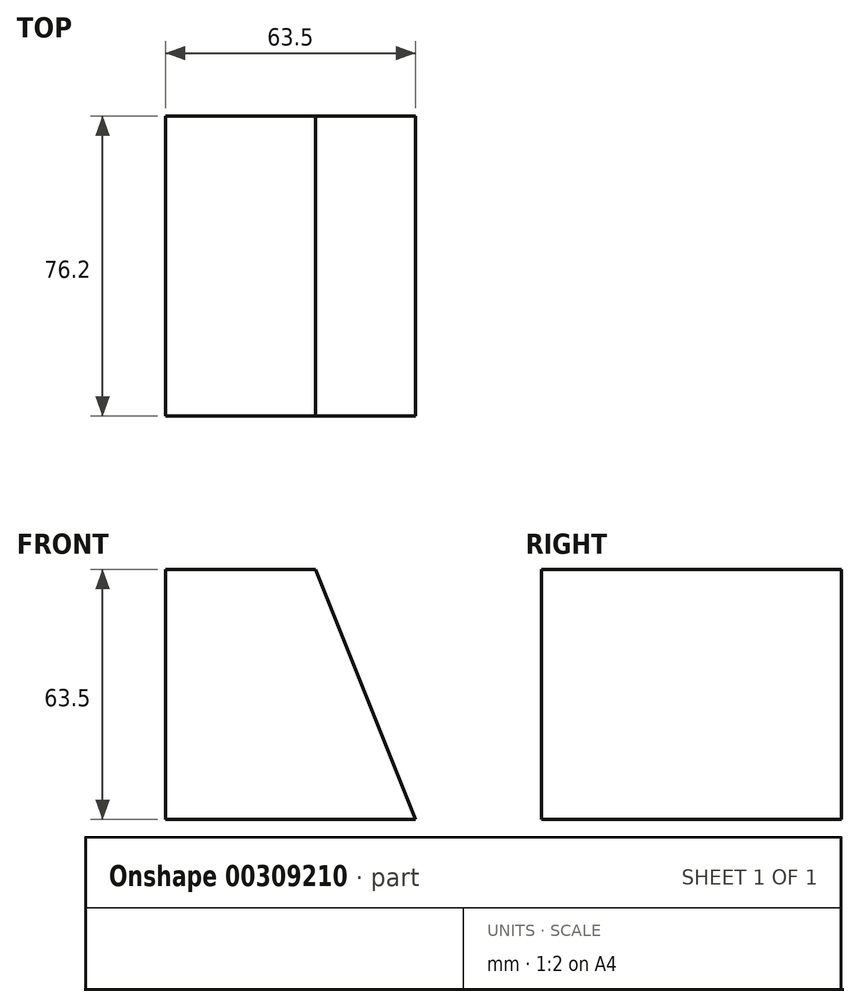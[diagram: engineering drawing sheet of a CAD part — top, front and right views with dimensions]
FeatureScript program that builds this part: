
annotation { "Feature Type Name" : "Feature", "Feature Type Description" : "" }
export const myFeature = defineFeature(function(context is Context, id is Id, definition is map)
    precondition{}
    {
        {
            var Q0;
            Q0=qCreatedBy(makeId("Front.planeOp"),FACE);
            var sketch = newSketch(context, id + "F0", { "sketchPlane" : qUnion([Q0])});
            skLineSegment(sketch, "E0", {"start": v(-22, 23.96) * mm, "end": v(-22, -39.54) * mm});
            skLineSegment(sketch, "E1", {"start": v(-22, -39.54) * mm, "end": v(41.5, -39.54) * mm});
            skLineSegment(sketch, "E2", {"start": v(41.5, -39.54) * mm, "end": v(16.1, 23.96) * mm});
            skLineSegment(sketch, "E3", {"start": v(16.1, 23.96) * mm, "end": v(-22, 23.96) * mm});
            skSolve(sketch);
        }
        {
            var Q0;
            Q0=makeQuery(id+"F0.imprint","IMPRINT",FACE,{"disambiguationData":[TD([[makeQuery(id+"F0.imprint","IMPRINT",EDGE,{"derivedFrom":sQuery(id+"F0.wireOp",EDGE,"E0")}),1.0]])]});
            extrude(context, id + "F1", {"entities" : qUnion([Q0]), "depth" : 76.2 * mm});
        }
    });
